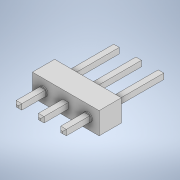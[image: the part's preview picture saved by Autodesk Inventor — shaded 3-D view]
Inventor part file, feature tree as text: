
AUTODESK INVENTOR PART (.ipt)
format: ipt  version: 2022 (Build 260153000, 153)  size: 186,880 bytes
history: native  units: mm
features: extrude x4, sketch x4, projected_geometry x3, chamfer x1
ambient origin geometry x8: Origin, YZ Plane, XZ Plane, XY Plane, X Axis, Y Axis, Z Axis, Center Point
bodies: Solid1 (feature_tree)
feature tree (12):
  extrude  "Extrusion1"  Depth=2.5mm
  extrude  "Extrusion2"  Depth=0.64mm
  extrude  "Extrusion3"  Depth=0.64mm
  chamfer  "Chamfer1"  Distance=2.54mm
  extrude  "Extrusion4"  Depth=2.54mm
  sketch  "Sketch1"  dims[d0=7.62mm d1=2.5mm]
  sketch  "Sketch2"  dims[d2=2.54mm d3=0.0mm d4=0.64mm]
  sketch  "Sketch3"  dims[d5=0.64mm d6=0.64mm]
  projected_geometry  "Projected Loop1"
  projected_geometry  "Projected Loop2"
  projected_geometry  "Projected Loop3"
  sketch  "Sketch4"  dims[d7=0.64mm d8=2.54mm d9=2.54mm d10=0.93mm d11=0.95mm d12=3.0mm d13=0.0mm d14=6.0mm d15=0.0mm d16=0.2mm d17=2.0mm d18=45.0deg d19=0.1mm d20=0.0mm d21=1.0mm d22=1.27mm d23=1.25mm d24=1.25mm d25=1.27mm]
